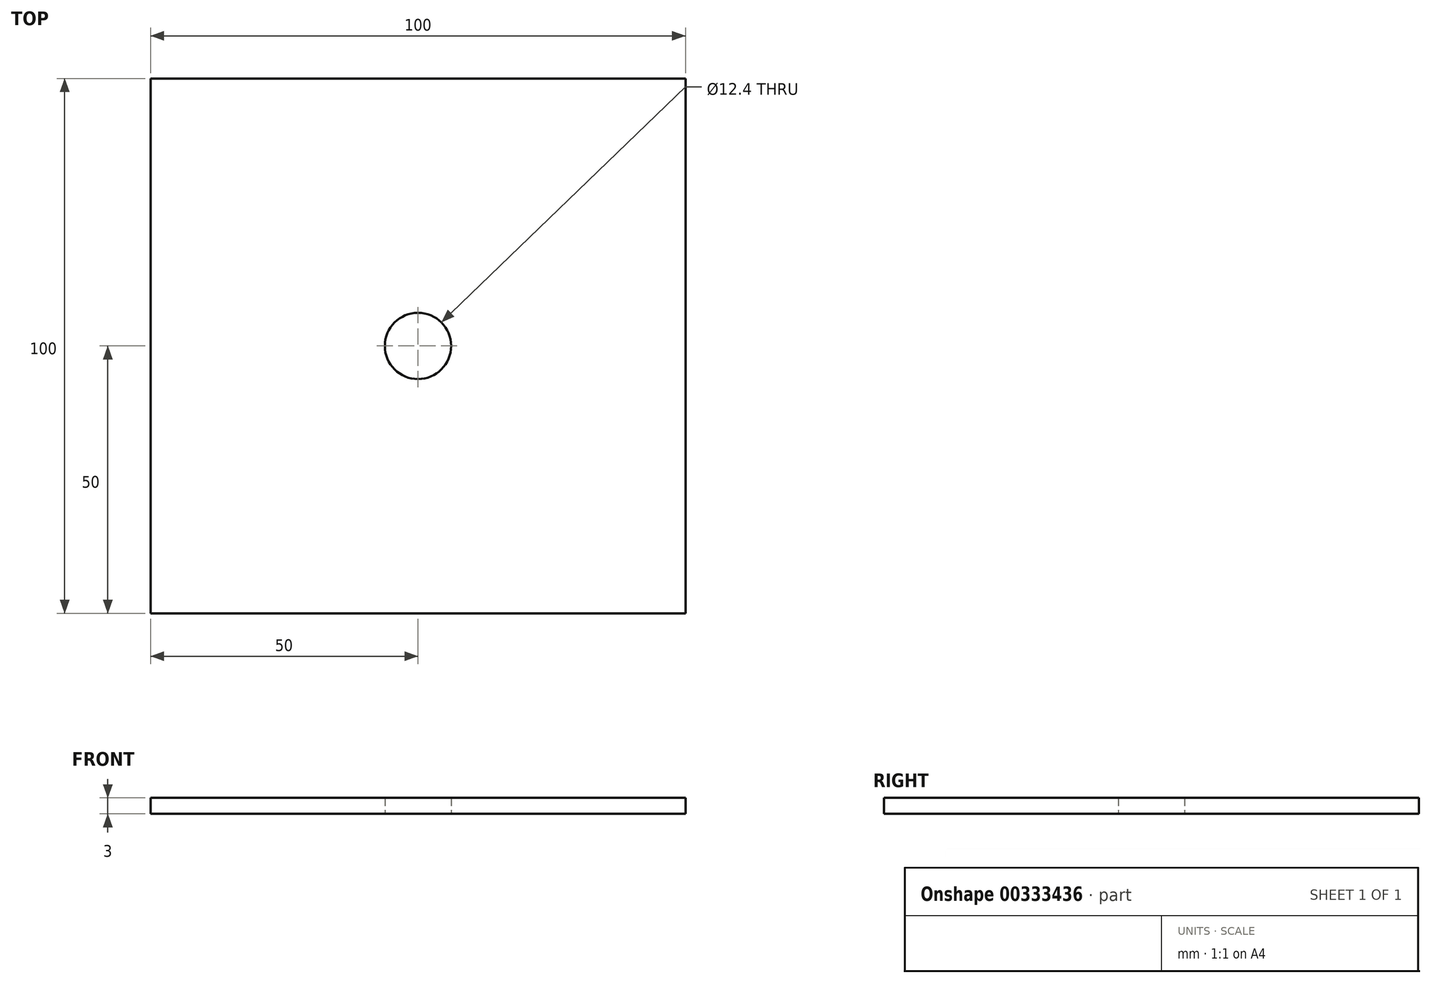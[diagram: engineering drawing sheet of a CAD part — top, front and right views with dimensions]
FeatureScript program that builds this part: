
annotation { "Feature Type Name" : "Feature", "Feature Type Description" : "" }
export const myFeature = defineFeature(function(context is Context, id is Id, definition is map)
    precondition{}
    {
        {
            var Q0;
            Q0=qCreatedBy(makeId("Top.planeOp"),FACE);
            var sketch = newSketch(context, id + "F0", { "sketchPlane" : qUnion([Q0])});
            skLineSegment(sketch, "E0.bottom", {"start": v(0, 0) * mm, "end": v(100, 0) * mm});
            skLineSegment(sketch, "E0.top", {"start": v(0, 100) * mm, "end": v(100, 100) * mm});
            skLineSegment(sketch, "E0.left", {"start": v(0, 0) * mm, "end": v(0, 100) * mm});
            skLineSegment(sketch, "E0.right", {"start": v(100, 0) * mm, "end": v(100, 100) * mm});
            skCircle(sketch, "E1", {"center": v(50, 50) * mm, "radius": 6.2 * mm});
            skSolve(sketch);
        }
        {
            var Q0;
            Q0=makeQuery(id+"F0.imprint","IMPRINT",FACE,{"disambiguationData":[TD([[makeQuery(id+"F0.imprint","IMPRINT",EDGE,{"derivedFrom":sQuery(id+"F0.wireOp",EDGE,"E0.bottom")}),1.0]])]});
            extrude(context, id + "F1", {"entities" : qUnion([Q0]), "depth" : 3 * mm});
        }
    });
